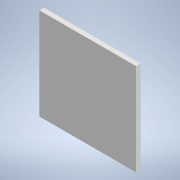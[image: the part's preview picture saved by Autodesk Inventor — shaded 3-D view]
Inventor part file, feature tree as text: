
AUTODESK INVENTOR PART (.ipt)
format: ipt  version: 2022 (Build 260153000, 153)  size: 89,088 bytes
history: native  units: mm
features: extrude x1, sketch x1
ambient origin geometry x8: Origin, YZ Plane, XZ Plane, XY Plane, X Axis, Y Axis, Z Axis, Center Point
bodies: Solid1 (feature_tree)
feature tree (2):
  extrude  "Extrusion1"  Depth=100.0mm
  sketch  "Sketch1"  dims[d0=105.0mm d1=100.0mm d2=5.0mm d3=0.0mm]
